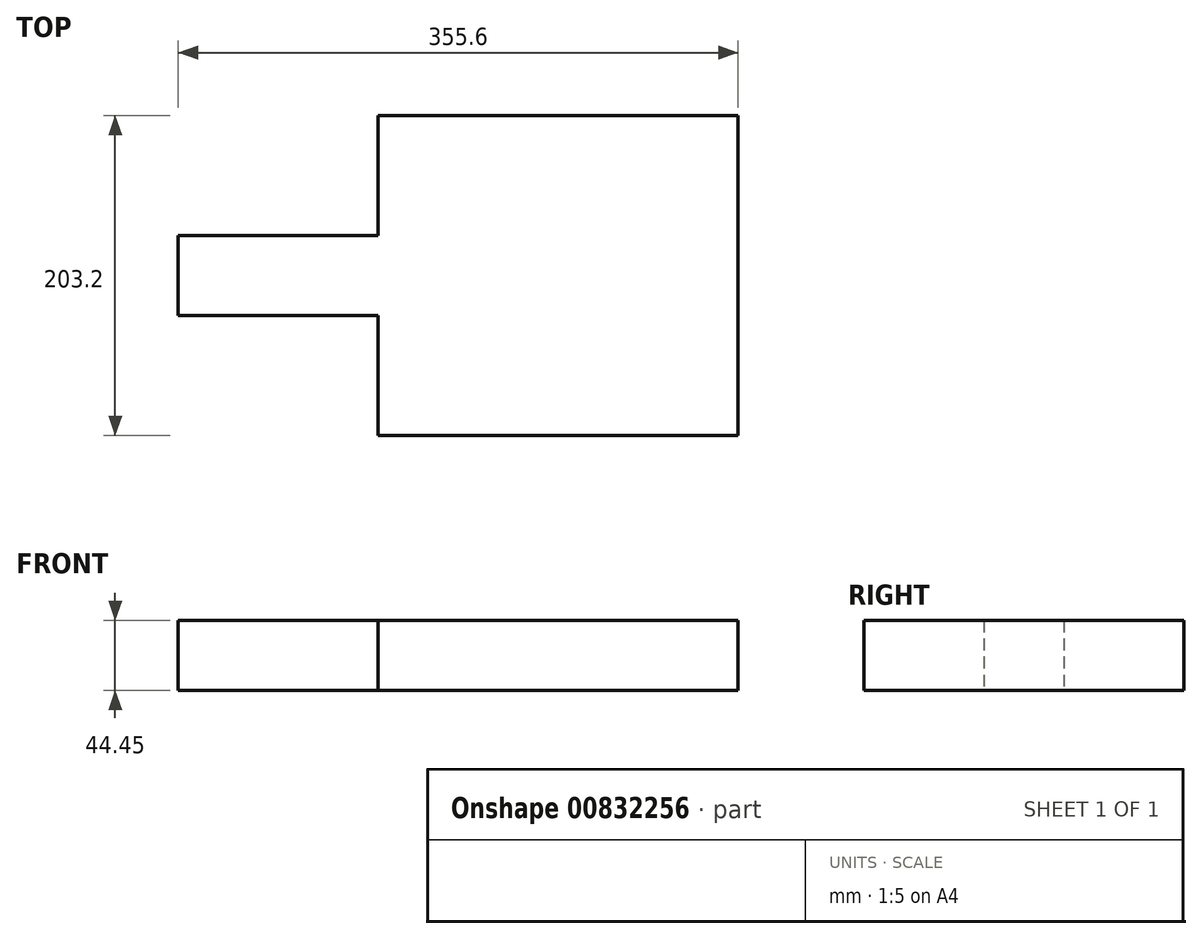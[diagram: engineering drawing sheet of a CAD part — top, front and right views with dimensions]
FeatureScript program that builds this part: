
annotation { "Feature Type Name" : "Feature", "Feature Type Description" : "" }
export const myFeature = defineFeature(function(context is Context, id is Id, definition is map)
    precondition{}
    {
        {
            var Q0;
            Q0=qCreatedBy(makeId("Top.planeOp"),FACE);
            var sketch = newSketch(context, id + "F0", { "sketchPlane" : qUnion([Q0])});
            skLineSegment(sketch, "E0.bottom", {"start": v(0, 0) * mm, "end": v(228.6, 0) * mm});
            skLineSegment(sketch, "E0.top", {"start": v(0, 203.2) * mm, "end": v(228.6, 203.2) * mm});
            skLineSegment(sketch, "E0.left", {"start": v(0, 0) * mm, "end": v(0, 203.2) * mm});
            skLineSegment(sketch, "E0.right", {"start": v(228.6, 0) * mm, "end": v(228.6, 203.2) * mm});
            skLineSegment(sketch, "E1.bottom", {"start": v(0, 127) * mm, "end": v(-127, 127) * mm});
            skLineSegment(sketch, "E1.top", {"start": v(0, 76.2) * mm, "end": v(-127, 76.2) * mm});
            skLineSegment(sketch, "E1.left", {"start": v(0, 127) * mm, "end": v(0, 76.2) * mm});
            skLineSegment(sketch, "E1.right", {"start": v(-127, 127) * mm, "end": v(-127, 76.2) * mm});
            skSolve(sketch);
        }
        {
            var Q0;
            {var subQ3=sQuery(id+"F0.wireOp",EDGE,"E0.bottom");Q0=makeQuery(id+"F0.imprint","IMPRINT",FACE,{"disambiguationData":[TD([[makeQuery(id+"F0.imprint","IMPRINT",EDGE,{"derivedFrom":subQ3}),1.0]])]});}
            var Q1;
            Q1=makeQuery(id+"F0.imprint","IMPRINT",FACE,{"disambiguationData":[TD([[makeQuery(id+"F0.imprint","IMPRINT",EDGE,{"derivedFrom":sQuery(id+"F0.wireOp",EDGE,"E1.bottom")}),1.0]])]});
            extrude(context, id + "F1", {"entities" : qUnion([Q0, Q1]), "depth" : 25.4 * mm, "offsetDistance" : 25.4 * mm, "hasSecondDirection" : true, "secondDirectionOppositeDirection" : true, "secondDirectionDepth" : 19.05 * mm});
        }
    });
